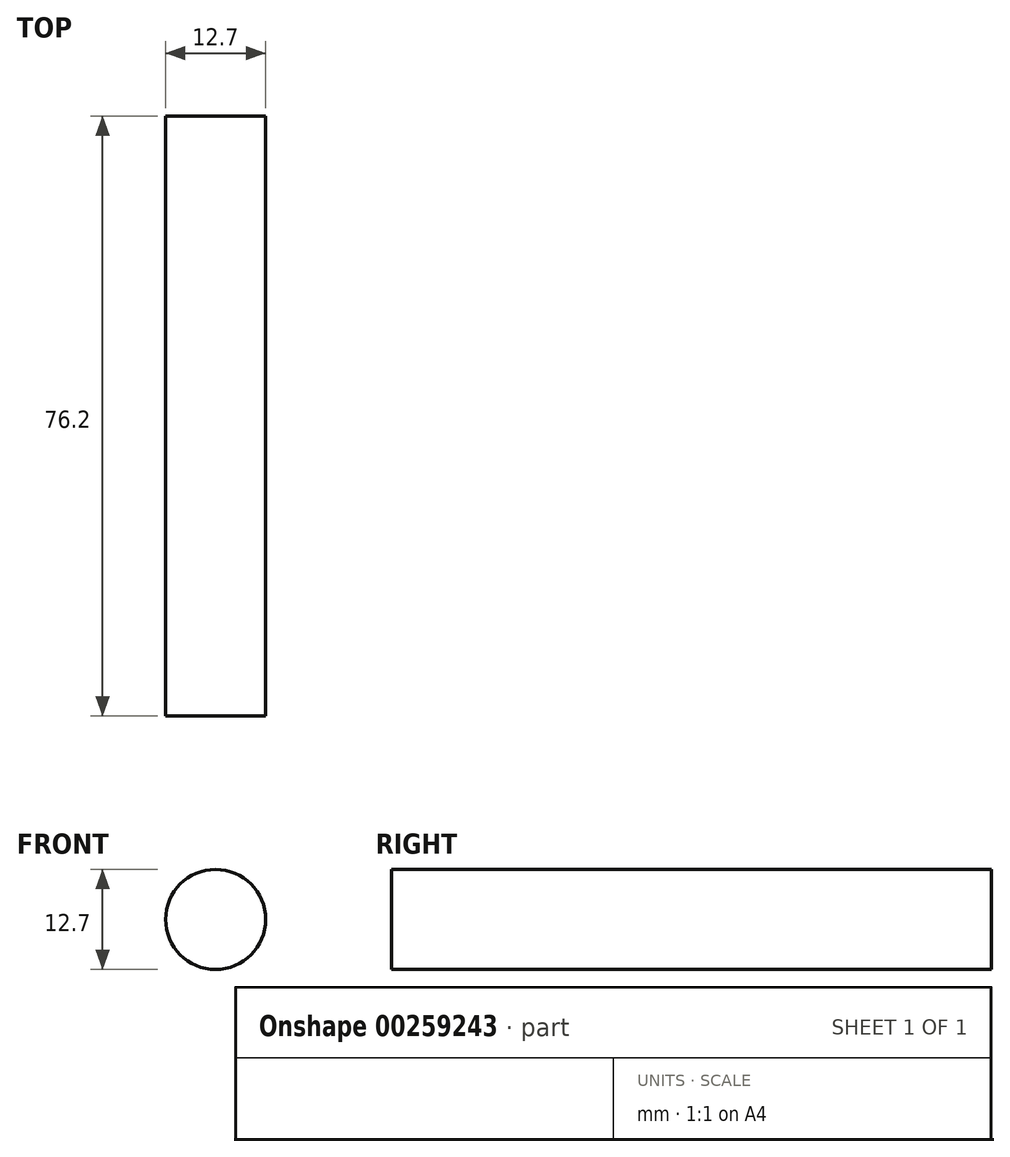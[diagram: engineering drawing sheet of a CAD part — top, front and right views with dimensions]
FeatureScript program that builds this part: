
annotation { "Feature Type Name" : "Feature", "Feature Type Description" : "" }
export const myFeature = defineFeature(function(context is Context, id is Id, definition is map)
    precondition{}
    {
        {
            var Q0;
            Q0=qCreatedBy(makeId("Front.planeOp"),FACE);
            var sketch = newSketch(context, id + "F0", { "sketchPlane" : qUnion([Q0])});
            skCircle(sketch, "E0", {"center": v(-4.53, 0) * mm, "radius": 6.35 * mm});
            skSolve(sketch);
        }
        {
            var Q0;
            Q0=makeQuery(id+"F0.imprint","IMPRINT",FACE,{"disambiguationData":[TD([[makeQuery(id+"F0.imprint","IMPRINT",EDGE,{"derivedFrom":sQuery(id+"F0.wireOp",EDGE,"E0")}),1.0]])]});
            extrude(context, id + "F1", {"entities" : qUnion([Q0]), "depth" : 76.2 * mm});
        }
    });
